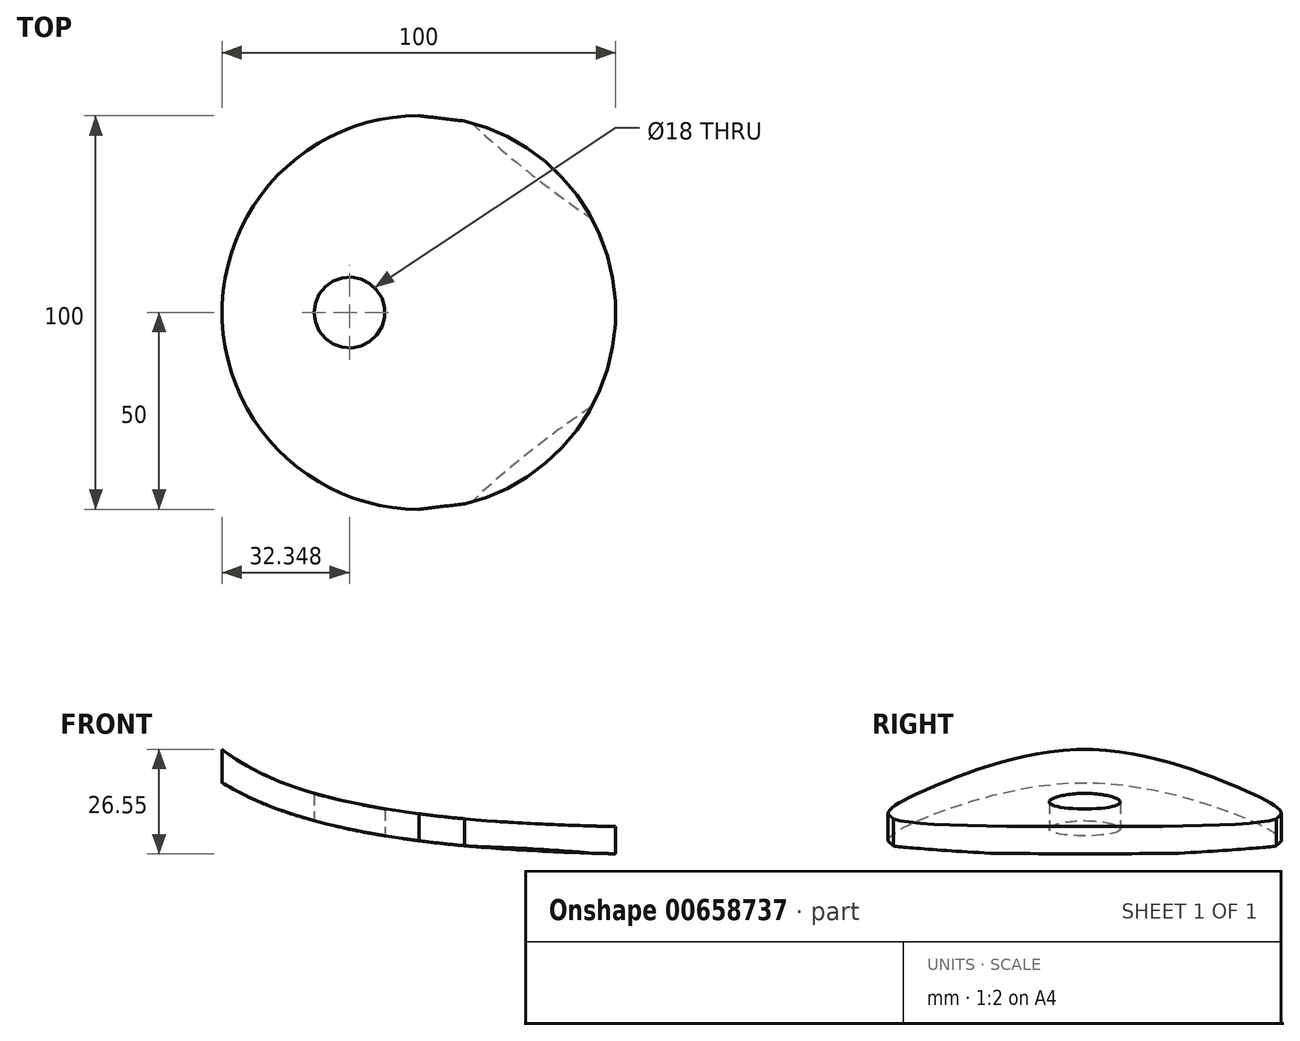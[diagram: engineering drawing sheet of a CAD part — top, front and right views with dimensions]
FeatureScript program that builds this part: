
annotation { "Feature Type Name" : "Feature", "Feature Type Description" : "" }
export const myFeature = defineFeature(function(context is Context, id is Id, definition is map)
    precondition{}
    {
        {
            var Q0;
            Q0=qCreatedBy(makeId("Top.planeOp"),FACE);
            var sketch = newSketch(context, id + "F0", { "sketchPlane" : qUnion([Q0])});
            skLineSegment(sketch, "E0.bottom", {"start": v(150, -50) * mm, "end": v(-150, -50) * mm});
            skLineSegment(sketch, "E0.top", {"start": v(150, 50) * mm, "end": v(-150, 50) * mm});
            skLineSegment(sketch, "E0.left", {"start": v(150, -50) * mm, "end": v(150, 50) * mm});
            skLineSegment(sketch, "E0.right", {"start": v(-150, -50) * mm, "end": v(-150, 50) * mm});
            skPoint(sketch, "E0.middle", {"position": v(0, 0) * mm});
            skCircle(sketch, "E1", {"center": v(-100, 0) * mm, "radius": 50 * mm});
            skPoint(sketch, "E1.centerSnap0", {"position": v(-150, 0) * mm});
            skLineSegment(sketch, "E2", {"start": v(150, 0) * mm, "end": v(150, 25.02) * mm});
            skLineSegment(sketch, "E3", {"start": v(150, 0) * mm, "end": v(150, -25.02) * mm});
            skArc(sketch, "E4", {"start": v(-100, 50) * mm, "mid": v(19.8, 39.06) * mm, "end": v(140.05, 35.02) * mm});
            skArc(sketch, "E5.MirrorCS", {"start": v(-100, -50) * mm, "mid": v(19.8, -39.06) * mm, "end": v(140.05, -35.02) * mm});
            skPoint(sketch, "E6.visualSharp", {"position": v(150, 35) * mm});
            skArc(sketch, "E6.filletArc", {"start": v(150, 25.02) * mm, "mid": v(147.09, 32.08) * mm, "end": v(140.05, 35.02) * mm});
            skPoint(sketch, "E7.visualSharp", {"position": v(150, -35) * mm});
            skArc(sketch, "E7.filletArc", {"start": v(140.05, -35.02) * mm, "mid": v(147.09, -32.08) * mm, "end": v(150, -25.02) * mm});
            skCircle(sketch, "E8", {"center": v(-117.65, 0) * mm, "radius": 9 * mm});
            skSolve(sketch);
        }
        {
            var Q0;
            Q0=qCreatedBy(makeId("Front.planeOp"),FACE);
            var sketch = newSketch(context, id + "F1", { "sketchPlane" : qUnion([Q0])});
            skFitSpline(sketch, "E9", {"points": [v(-154.18, 21.33) * mm, v(0, 0) * mm, v(151.57, 0) * mm], "startDerivative": vector(168.27, -127.12) * mm, "endDerivative": vector(127.49, 0) * mm});
            skFitSpline(sketch, "E10.0", {"points": [v(-149.96, 26.91) * mm, v(-148.45, 25.77) * mm, v(-145.16, 23.6) * mm, v(-137.5, 19.66) * mm, v(-126.02, 15.58) * mm, v(-109.56, 11.98) * mm, v(-90.85, 9.52) * mm, v(-70.3, 8.03) * mm, v(-48.28, 7.27) * mm, v(-29.03, 7.05) * mm, v(-13.26, 7) * mm, v(-1.3, 7) * mm, v(10.77, 7) * mm, v(26.85, 7) * mm, v(46.8, 7) * mm, v(69.88, 7) * mm, v(98.76, 7) * mm, v(129.85, 7) * mm, v(146.26, 7) * mm, v(151.57, 7) * mm]});
            skLineSegment(sketch, "E11", {"start": v(151.57, 7) * mm, "end": v(151.57, 0) * mm, "construction": true});
            skLineSegment(sketch, "E12", {"start": v(-154.18, 21.33) * mm, "end": v(-149.96, 26.91) * mm, "construction": true});
            skArc(sketch, "E13", {"start": v(-154.18, 21.33) * mm, "mid": v(-154.86, 26.23) * mm, "end": v(-149.96, 26.91) * mm});
            skArc(sketch, "E14", {"start": v(151.57, 7) * mm, "mid": v(155.07, 3.5) * mm, "end": v(151.57, 0) * mm});
            skSolve(sketch);
        }
        {
            var Q0;
            Q0=makeQuery(id+"F1.imprint","IMPRINT",FACE,{"disambiguationData":[TD([[makeQuery(id+"F1.imprint","IMPRINT",EDGE,{"derivedFrom":sQuery(id+"F1.wireOp",EDGE,"E9")}),1.0]])]});
            extrude(context, id + "F2", {"entities" : qUnion([Q0]), "endBound" : BoundingType.SYMMETRIC, "depth" : 100 * mm, "offsetDistance" : 25 * mm});
        }
        {
            var Q0;
            {var subQ0=sQuery(id+"F0.wireOp",EDGE,"E4");var subQ1=sQuery(id+"F0.wireOp",EDGE,"E1");var subQ2=makeQuery(id+"F0.imprint","INTERSECT",VERTEX,{"derivedFrom":[subQ1,subQ0]});Q0=makeQuery(id+"F0.imprint","IMPRINT",FACE,{"disambiguationData":[TD([[makeQuery(id+"F0.imprint","IMPRINT",EDGE,{"disambiguationData":[TD([[subQ2,1.0]])],"derivedFrom":subQ1}),1.0]])]});}
            var Q1;
            Q1=makeQuery(id+"F0.imprint","IMPRINT",FACE,{"disambiguationData":[TD([[makeQuery(id+"F0.imprint","IMPRINT",EDGE,{"derivedFrom":sQuery(id+"F0.wireOp",EDGE,"E2")}),1.0]])]});
            extrude(context, id + "F3", {"entities" : qUnion([Q0, Q1]), "operationType" : NewBodyOperationType.INTERSECT, "depth" : 41 * mm, "offsetDistance" : 25 * mm});
        }
        {
            var Q0;
            Q0=qCreatedBy(makeId("Right.planeOp"),FACE);
            var sketch = newSketch(context, id + "F4", { "sketchPlane" : qUnion([Q0])});
            skLineSegment(sketch, "E15", {"start": v(-55.38, 3.04) * mm, "end": v(0, 3.04) * mm, "construction": true});
            skLineSegment(sketch, "E16.MirrorCS", {"start": v(55.38, 3.04) * mm, "end": v(0, 3.04) * mm, "construction": true});
            skArc(sketch, "E17", {"start": v(-55.38, 3.04) * mm, "mid": v(0, 0) * mm, "end": v(55.38, 3.04) * mm});
            skArc(sketch, "E18.0", {"start": v(-52.1, 32.86) * mm, "mid": v(0, 30) * mm, "end": v(52.1, 32.86) * mm});
            skLineSegment(sketch, "E19", {"start": v(-52.1, 32.86) * mm, "end": v(-55.38, 3.04) * mm});
            skLineSegment(sketch, "E20", {"start": v(52.1, 32.86) * mm, "end": v(55.38, 3.04) * mm});
            skSolve(sketch);
        }
        {
            var Q0;
            Q0=makeQuery(id+"F4.imprint","IMPRINT",FACE,{"disambiguationData":[TD([[makeQuery(id+"F4.imprint","IMPRINT",EDGE,{"derivedFrom":sQuery(id+"F4.wireOp",EDGE,"E17")}),1.0]])]});
            extrude(context, id + "F5", {"entities" : qUnion([Q0]), "operationType" : NewBodyOperationType.INTERSECT, "endBound" : BoundingType.SYMMETRIC, "depth" : 300 * mm, "offsetDistance" : 25 * mm});
        }
    });
